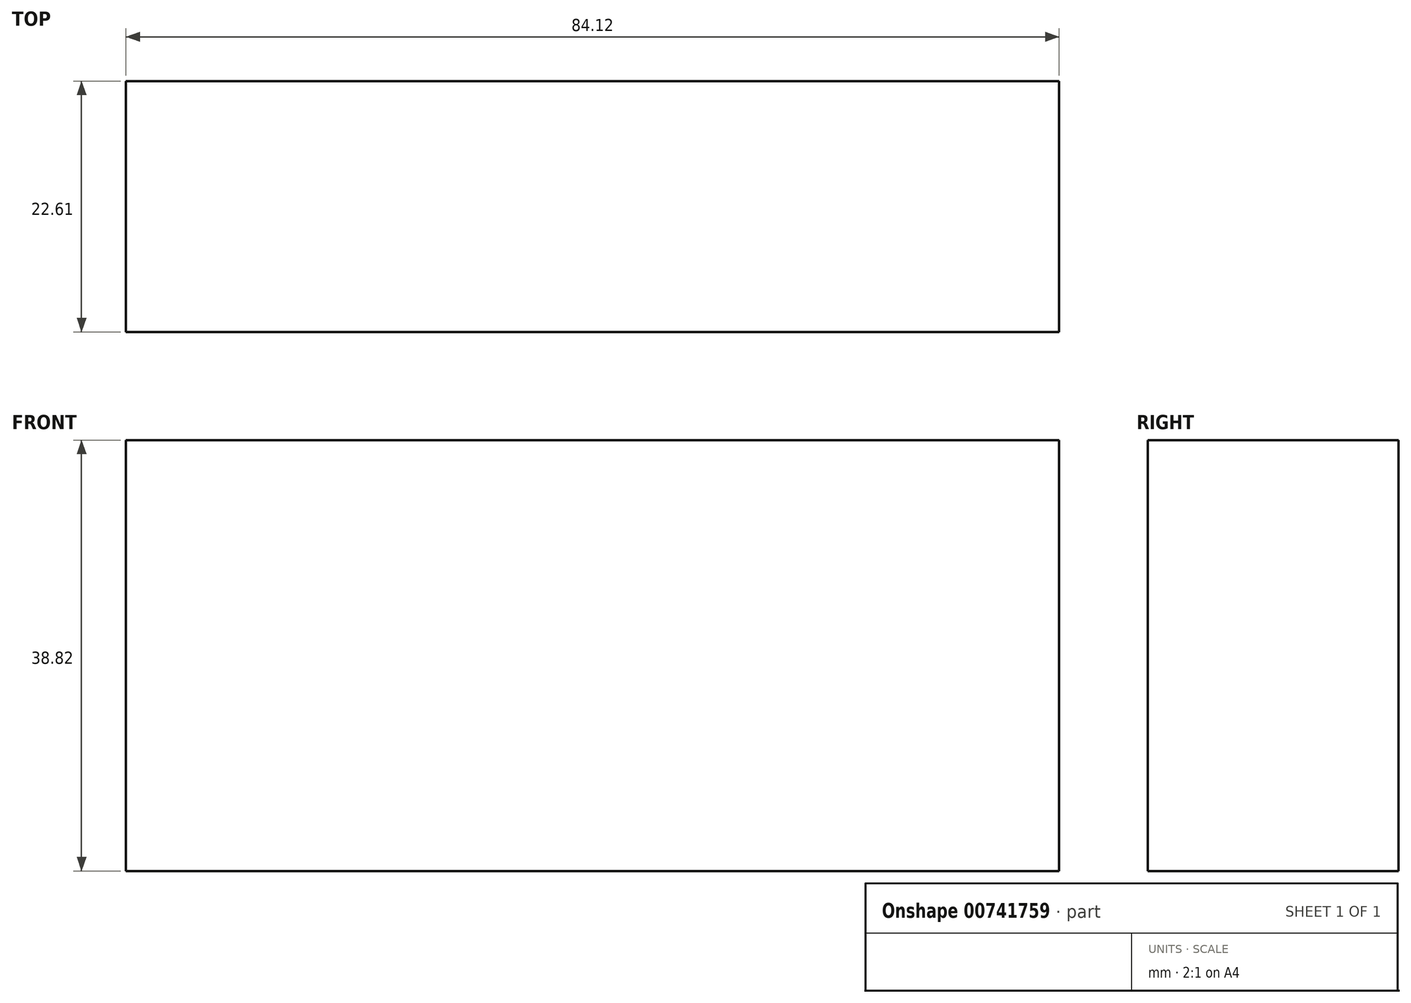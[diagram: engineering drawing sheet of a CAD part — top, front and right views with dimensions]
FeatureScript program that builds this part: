
annotation { "Feature Type Name" : "Feature", "Feature Type Description" : "" }
export const myFeature = defineFeature(function(context is Context, id is Id, definition is map)
    precondition{}
    {
        {
            var Q0;
            Q0=qCreatedBy(makeId("Front.planeOp"),FACE);
            var sketch = newSketch(context, id + "F0", { "sketchPlane" : qUnion([Q0])});
            skLineSegment(sketch, "E0", {"start": v(0, 0) * mm, "end": v(84.12, 0) * mm});
            skLineSegment(sketch, "E1", {"start": v(84.12, 0) * mm, "end": v(84.12, -38.82) * mm});
            skLineSegment(sketch, "E2", {"start": v(84.12, -38.82) * mm, "end": v(0, -38.82) * mm});
            skLineSegment(sketch, "E3", {"start": v(0, -38.82) * mm, "end": v(0, 0) * mm});
            skSolve(sketch);
        }
        {
            var Q0;
            Q0=makeQuery(id+"F0.imprint","IMPRINT",FACE,{"disambiguationData":[TD([[makeQuery(id+"F0.imprint","IMPRINT",EDGE,{"derivedFrom":sQuery(id+"F0.wireOp",EDGE,"E0")}),-1.0]])]});
            extrude(context, id + "F1", {"entities" : qUnion([Q0]), "depth" : 22.6 * mm, "offsetDistance" : 25.4 * mm});
        }
    });
